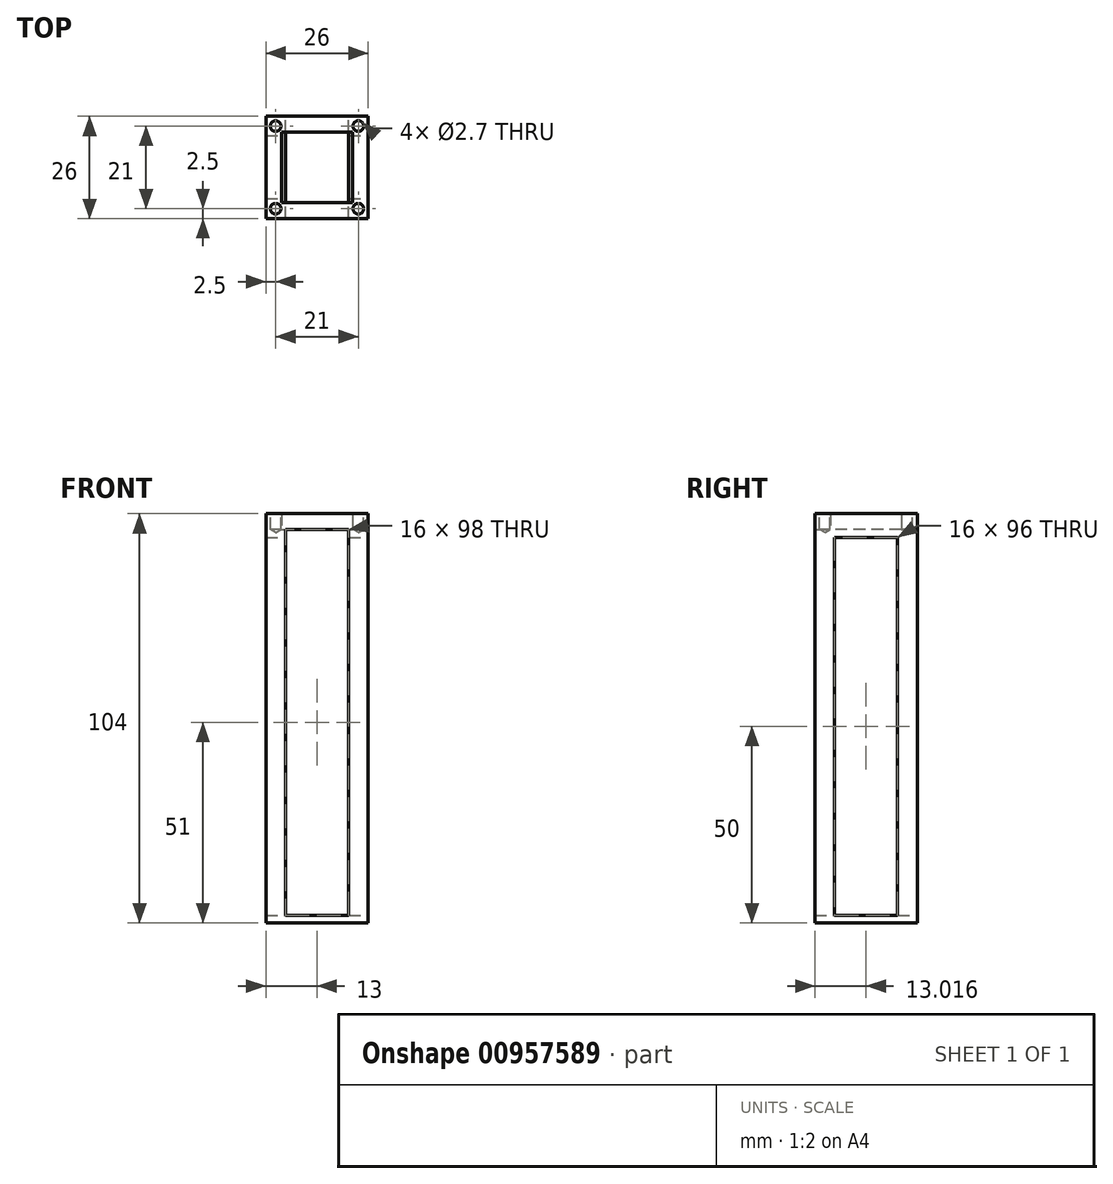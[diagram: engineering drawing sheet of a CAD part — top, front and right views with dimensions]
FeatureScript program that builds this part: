
annotation { "Feature Type Name" : "Feature", "Feature Type Description" : "" }
export const myFeature = defineFeature(function(context is Context, id is Id, definition is map)
    precondition{}
    {
        {
            var Q0;
            Q0=qCreatedBy(makeId("Top.planeOp"),FACE);
            var sketch = newSketch(context, id + "F0", { "sketchPlane" : qUnion([Q0])});
            skLineSegment(sketch, "E0.bottom", {"start": v(13, 13) * mm, "end": v(-13, 13) * mm});
            skLineSegment(sketch, "E0.top", {"start": v(13, -13) * mm, "end": v(-13, -13) * mm});
            skLineSegment(sketch, "E0.left", {"start": v(13, 13) * mm, "end": v(13, -13) * mm});
            skLineSegment(sketch, "E0.right", {"start": v(-13, 13) * mm, "end": v(-13, -13) * mm});
            skPoint(sketch, "E0.middle", {"position": v(0, 0) * mm});
            skLineSegment(sketch, "E1.bottom", {"start": v(8, 8) * mm, "end": v(-8, 8) * mm});
            skLineSegment(sketch, "E1.top", {"start": v(8, -8) * mm, "end": v(-8, -8) * mm});
            skLineSegment(sketch, "E1.left", {"start": v(8, 8) * mm, "end": v(8, -8) * mm});
            skLineSegment(sketch, "E1.right", {"start": v(-8, 8) * mm, "end": v(-8, -8) * mm});
            skSolve(sketch);
        }
        {
            var Q0;
            Q0=makeQuery(id+"F0.imprint","IMPRINT",FACE,{"disambiguationData":[TD([[makeQuery(id+"F0.imprint","IMPRINT",EDGE,{"derivedFrom":sQuery(id+"F0.wireOp",EDGE,"E0.bottom")}),1.0]])]});
            var Q1;
            Q1=makeQuery(id+"F0.imprint","IMPRINT",FACE,{"disambiguationData":[TD([[makeQuery(id+"F0.imprint","IMPRINT",EDGE,{"derivedFrom":sQuery(id+"F0.wireOp",EDGE,"E1.bottom")}),-1.0]])]});
            var Q2;
            Q2=makeQuery(id+"F0.imprint","IMPRINT",FACE,{"disambiguationData":[TD([[makeQuery(id+"F0.imprint","IMPRINT",EDGE,{"derivedFrom":sQuery(id+"F0.wireOp",EDGE,"E1.bottom")}),1.0]])]});
            extrude(context, id + "F1", {"entities" : qUnion([Q0, Q1, Q2]), "depth" : 2 * mm, "offsetDistance" : 25 * mm});
        }
        {
            var Q0;
            Q0=qSketchRegion(id+"F0",true);
            var Q1;
            Q1=makeQuery(id+"F0.imprint","IMPRINT",FACE,{"disambiguationData":[TD([[makeQuery(id+"F0.imprint","IMPRINT",EDGE,{"derivedFrom":sQuery(id+"F0.wireOp",EDGE,"E1.bottom")}),-1.0]])]});
            extrude(context, id + "F2", {"entities" : qUnion([Q0, Q1]), "operationType" : NewBodyOperationType.ADD, "depth" : 100 * mm, "offsetDistance" : 25 * mm});
        }
        {
            var Q0;
            Q0=makeQuery(id+"F2.opExtrude","CAP_FACE",FACE,{"disambiguationData":[OSD([sQuery(id+"F0.wireOp",EDGE,"E0.bottom"),sQuery(id+"F0.wireOp",EDGE,"E0.top"),sQuery(id+"F0.wireOp",EDGE,"E0.left"),sQuery(id+"F0.wireOp",EDGE,"E0.right"),sQuery(id+"F0.wireOp",EDGE,"E1.bottom"),sQuery(id+"F0.wireOp",EDGE,"E1.top"),sQuery(id+"F0.wireOp",EDGE,"E1.left"),sQuery(id+"F0.wireOp",EDGE,"E1.right")])],"isStart":false});
            var sketch = newSketch(context, id + "F3", { "sketchPlane" : qUnion([Q0])});
            skLineSegment(sketch, "E2.bottom", {"start": v(-9, 9) * mm, "end": v(9, 9) * mm});
            skLineSegment(sketch, "E2.top", {"start": v(-9, -9) * mm, "end": v(9, -9) * mm});
            skLineSegment(sketch, "E2.left", {"start": v(-9, 9) * mm, "end": v(-9, -9) * mm});
            skLineSegment(sketch, "E2.right", {"start": v(9, 9) * mm, "end": v(9, -9) * mm});
            skPoint(sketch, "E2.middle", {"position": v(0, 0) * mm});
            skSolve(sketch);
        }
        {
            var Q0;
            Q0=makeQuery(id+"F3.imprint","IMPRINT",FACE,{"disambiguationData":[TD([[makeQuery(id+"F3.imprint","IMPRINT",EDGE,{"derivedFrom":sQuery(id+"F3.wireOp",EDGE,"E2.bottom")}),1.0]])]});
            extrude(context, id + "F4", {"entities" : qUnion([Q0]), "operationType" : NewBodyOperationType.ADD, "depth" : 4 * mm, "offsetDistance" : 25 * mm});
        }
        {
            var Q0;
            Q0=makeQuery(id+"F4.opExtrude","CAP_FACE",FACE,{"disambiguationData":[OSD([sQuery(id+"F0.wireOp",EDGE,"E0.bottom"),sQuery(id+"F0.wireOp",EDGE,"E0.top"),sQuery(id+"F0.wireOp",EDGE,"E0.left"),sQuery(id+"F0.wireOp",EDGE,"E0.right"),sQuery(id+"F3.wireOp",EDGE,"E2.bottom"),sQuery(id+"F3.wireOp",EDGE,"E2.top"),sQuery(id+"F3.wireOp",EDGE,"E2.left"),sQuery(id+"F3.wireOp",EDGE,"E2.right")])],"isStart":false});
            var sketch = newSketch(context, id + "F5", { "sketchPlane" : qUnion([Q0])});
            skLineSegment(sketch, "E3", {"start": v(-2.5, 13) * mm, "end": v(-2.5, 9) * mm});
            skLineSegment(sketch, "E4.MirrorCS", {"start": v(2.5, 13) * mm, "end": v(2.5, 9) * mm});
            skLineSegment(sketch, "E5.MirrorCS", {"start": v(2.5, -13) * mm, "end": v(2.5, -9) * mm});
            skLineSegment(sketch, "E6.MirrorCS", {"start": v(-2.5, -13) * mm, "end": v(-2.5, -9) * mm});
            skLineSegment(sketch, "E7", {"start": v(-13, 13) * mm, "end": v(-9, 9) * mm, "construction": true});
            skPoint(sketch, "E8", {"position": v(-10.5, 10.5) * mm});
            skPoint(sketch, "E9.MirrorP", {"position": v(10.5, 10.5) * mm});
            skLineSegment(sketch, "E10.MirrorCS", {"start": v(13, 13) * mm, "end": v(9, 9) * mm, "construction": true});
            skLineSegment(sketch, "E11.MirrorCS", {"start": v(-13, -13) * mm, "end": v(-9, -9) * mm, "construction": true});
            skPoint(sketch, "E12.MirrorP", {"position": v(-10.5, -10.5) * mm});
            skLineSegment(sketch, "E13.MirrorCS", {"start": v(13, -13) * mm, "end": v(9, -9) * mm, "construction": true});
            skPoint(sketch, "E14.MirrorP", {"position": v(10.5, -10.5) * mm});
            skSolve(sketch);
        }
        {
            var Q0;
            Q0=sQuery(id+"F5.wireOp",VERTEX,"E8");
            var Q1;
            Q1=sQuery(id+"F5.wireOp",VERTEX,"E9.MirrorP");
            var Q2;
            Q2=sQuery(id+"F5.wireOp",VERTEX,"E12.MirrorP");
            var Q3;
            Q3=sQuery(id+"F5.wireOp",VERTEX,"E14.MirrorP");
            var Q4;
            Q4=makeQuery(id+"F1.opExtrude","SWEPT_BODY",BODY,{"disambiguationData":[OSD([sQuery(id+"F0.wireOp",EDGE,"E0.bottom"),sQuery(id+"F0.wireOp",EDGE,"E0.top"),sQuery(id+"F0.wireOp",EDGE,"E0.left"),sQuery(id+"F0.wireOp",EDGE,"E0.right")])]});
            hole(context, id + "F6", {"style" : HoleStyle.SIMPLE, "endStyle" : HoleEndStyle.BLIND, "standardTappedOrClearance" : lookupTablePath({ "standard" : "ISO", "engagement" : "50%", "pitch" : "0.5 mm", "size" : "M3", "type" : "Tapped" }), "standardBlindInLast" : lookupTablePath({ "standard" : "ISO", "fit" : "Normal", "engagement" : "50%", "pitch" : "0.5 mm", "size" : "M3", "type" : "Clearance & tapped" }), "holeDiameter" : 2.7 * mm, "majorDiameter" : 3 * mm, "showTappedDepth" : true, "holeDepth" : 4 * mm, "isTappedThrough" : true, "tappedDepth" : 2.5 * mm, "tapClearance" : 3, "locations" : qUnion([Q0, Q1, Q2, Q3]), "scope" : qUnion([Q4])});
        }
        {
            var Q0;
            {var subQ0=sQuery(id+"F0.wireOp",EDGE,"E0.left");Q0=makeQuery(id+"F4.boolean.opBoolean","MERGE",FACE,{"derivedFrom":[makeQuery(id+"F2.boolean.opBoolean","MERGE",FACE,{"derivedFrom":[makeQuery(id+"F1.opExtrude","SWEPT_FACE",FACE,{"disambiguationData":[OSD([subQ0])]}),makeQuery(id+"F2.opExtrude","SWEPT_FACE",FACE,{"disambiguationData":[OSD([subQ0])]})]}),makeQuery(id+"F4.opExtrude","SWEPT_FACE",FACE,{"disambiguationData":[OSD([subQ0])]})]});}
            var sketch = newSketch(context, id + "F7", { "sketchPlane" : qUnion([Q0])});
            skLineSegment(sketch, "E15.bottom", {"start": v(-7.98, 98) * mm, "end": v(8.02, 98) * mm});
            skLineSegment(sketch, "E15.top", {"start": v(-7.98, 2) * mm, "end": v(8.02, 2) * mm});
            skLineSegment(sketch, "E15.left", {"start": v(-7.98, 98) * mm, "end": v(-7.98, 2) * mm});
            skLineSegment(sketch, "E15.right", {"start": v(8.02, 98) * mm, "end": v(8.02, 2) * mm});
            skLineSegment(sketch, "E16", {"start": v(-7.98, 0) * mm, "end": v(-7.98, 100) * mm, "construction": true});
            skLineSegment(sketch, "E17", {"start": v(8.02, 0) * mm, "end": v(8.02, 100) * mm, "construction": true});
            skSolve(sketch);
        }
        {
            var Q0;
            Q0=makeQuery(id+"F7.imprint","IMPRINT",FACE,{"disambiguationData":[TD([[makeQuery(id+"F7.imprint","IMPRINT",EDGE,{"derivedFrom":sQuery(id+"F7.wireOp",EDGE,"E15.bottom")}),-1.0]])]});
            extrude(context, id + "F8", {"entities" : qUnion([Q0]), "operationType" : NewBodyOperationType.REMOVE, "endBound" : BoundingType.THROUGH_ALL, "oppositeDirection" : true, "depth" : 25 * mm, "offsetDistance" : 25 * mm});
        }
        {
            var Q0;
            {var subQ0=sQuery(id+"F0.wireOp",EDGE,"E0.bottom");Q0=makeQuery(id+"F4.boolean.opBoolean","MERGE",FACE,{"derivedFrom":[makeQuery(id+"F2.boolean.opBoolean","MERGE",FACE,{"derivedFrom":[makeQuery(id+"F1.opExtrude","SWEPT_FACE",FACE,{"disambiguationData":[OSD([subQ0])]}),makeQuery(id+"F2.opExtrude","SWEPT_FACE",FACE,{"disambiguationData":[OSD([subQ0])]})]}),makeQuery(id+"F4.opExtrude","SWEPT_FACE",FACE,{"disambiguationData":[OSD([subQ0])]})]});}
            var sketch = newSketch(context, id + "F9", { "sketchPlane" : qUnion([Q0])});
            skLineSegment(sketch, "E18.bottom", {"start": v(-8, 100) * mm, "end": v(8, 100) * mm});
            skLineSegment(sketch, "E18.top", {"start": v(-8, 2) * mm, "end": v(8, 2) * mm});
            skLineSegment(sketch, "E18.left", {"start": v(-8, 100) * mm, "end": v(-8, 2) * mm});
            skLineSegment(sketch, "E18.right", {"start": v(8, 100) * mm, "end": v(8, 2) * mm});
            skLineSegment(sketch, "E19", {"start": v(-8, 0) * mm, "end": v(-8, 10) * mm, "construction": true});
            skLineSegment(sketch, "E20", {"start": v(8, 0) * mm, "end": v(8, 10) * mm, "construction": true});
            skSolve(sketch);
        }
        {
            var Q0;
            Q0 = qSketchRegion(id + "F9", true);
            extrude(context, id + "F10", {"entities" : qUnion([Q0]), "operationType" : NewBodyOperationType.REMOVE, "endBound" : BoundingType.THROUGH_ALL, "oppositeDirection" : true, "depth" : 25 * mm, "offsetDistance" : 25 * mm});
        }
    });
